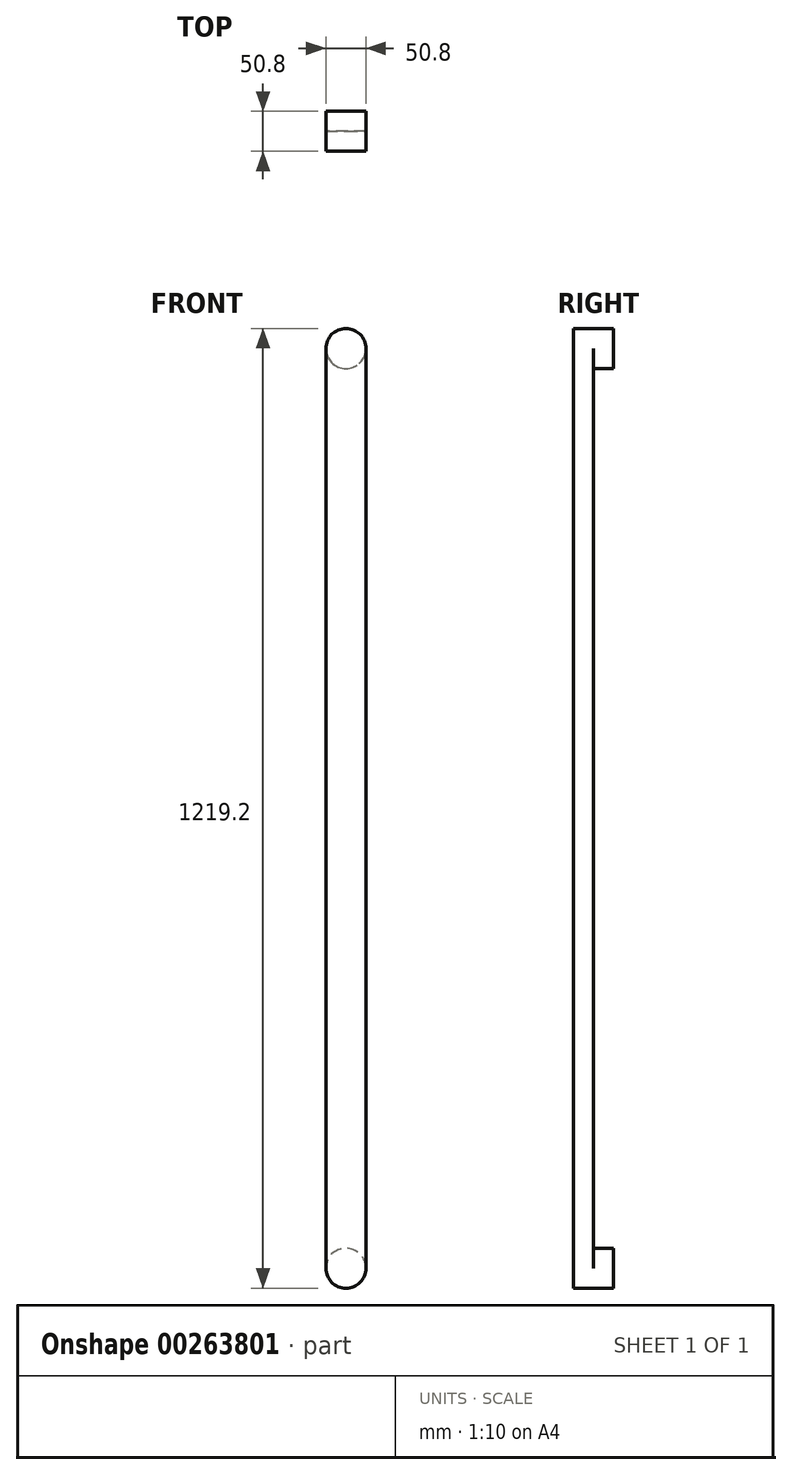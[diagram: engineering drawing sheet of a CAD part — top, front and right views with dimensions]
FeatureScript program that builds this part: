
annotation { "Feature Type Name" : "Feature", "Feature Type Description" : "" }
export const myFeature = defineFeature(function(context is Context, id is Id, definition is map)
    precondition{}
    {
        {
            var Q0;
            Q0=qCreatedBy(makeId("Front.planeOp"),FACE);
            var sketch = newSketch(context, id + "F0", { "sketchPlane" : qUnion([Q0])});
            skLineSegment(sketch, "E0.bottom", {"start": v(25.4, 609.6) * mm, "end": v(-25.4, 609.6) * mm});
            skLineSegment(sketch, "E0.top", {"start": v(25.4, -609.6) * mm, "end": v(-25.4, -609.6) * mm});
            skLineSegment(sketch, "E0.left", {"start": v(25.4, 609.6) * mm, "end": v(25.4, -609.6) * mm});
            skLineSegment(sketch, "E0.right", {"start": v(-25.4, 609.6) * mm, "end": v(-25.4, -609.6) * mm});
            skPoint(sketch, "E0.middle", {"position": v(0, 0) * mm});
            skCircle(sketch, "E1", {"center": v(0, 584.2) * mm, "radius": 25.4 * mm});
            skPoint(sketch, "E1.first.point", {"position": v(0, 609.6) * mm});
            skPoint(sketch, "E1.second.point", {"position": v(-25.4, 584.2) * mm});
            skPoint(sketch, "E1.third.point", {"position": v(25.4, 584.2) * mm});
            skCircle(sketch, "E2", {"center": v(0, -584.2) * mm, "radius": 25.4 * mm});
            skPoint(sketch, "E2.first.point", {"position": v(0, -609.6) * mm});
            skPoint(sketch, "E2.second.point", {"position": v(-25.4, -584.2) * mm});
            skPoint(sketch, "E2.third.point", {"position": v(25.4, -584.2) * mm});
            skSolve(sketch);
        }
        {
            var Q0;
            {var subQ0=sQuery(id+"F0.wireOp",EDGE,"E1");var subQ1=sQuery(id+"F0.wireOp",EDGE,"E0.left");var subQ2=makeQuery(id+"F0.imprint","INTERSECT",VERTEX,{"derivedFrom":[subQ1,subQ0]});Q0=makeQuery(id+"F0.imprint","IMPRINT",FACE,{"disambiguationData":[TD([[makeQuery(id+"F0.imprint","IMPRINT",EDGE,{"disambiguationData":[TD([[subQ2,-1.0]])],"derivedFrom":subQ1}),-1.0]])]});}
            extrude(context, id + "F1", {"entities" : qUnion([Q0]), "oppositeDirection" : true, "depth" : 25.4 * mm});
        }
        {
            var Q0;
            {var subQ0=sQuery(id+"F0.wireOp",EDGE,"E1");var subQ1=makeQuery(id+"F0.imprint","INTERSECT",VERTEX,{"derivedFrom":[sQuery(id+"F0.wireOp",EDGE,"E0.bottom"),subQ0]});Q0=makeQuery(id+"F0.imprint","IMPRINT",FACE,{"disambiguationData":[TD([[makeQuery(id+"F0.imprint","IMPRINT",EDGE,{"disambiguationData":[TD([[subQ1,1.0]])],"derivedFrom":subQ0}),1.0]])]});}
            var Q1;
            {var subQ0=sQuery(id+"F0.wireOp",EDGE,"E2");var subQ1=makeQuery(id+"F0.imprint","INTERSECT",VERTEX,{"derivedFrom":[sQuery(id+"F0.wireOp",EDGE,"E0.left"),subQ0]});Q1=makeQuery(id+"F0.imprint","IMPRINT",FACE,{"disambiguationData":[TD([[makeQuery(id+"F0.imprint","IMPRINT",EDGE,{"disambiguationData":[TD([[subQ1,-1.0]])],"derivedFrom":subQ0}),1.0]])]});}
            extrude(context, id + "F2", {"entities" : qUnion([Q0, Q1]), "operationType" : NewBodyOperationType.ADD, "oppositeDirection" : true, "depth" : 50.8 * mm});
        }
    });
